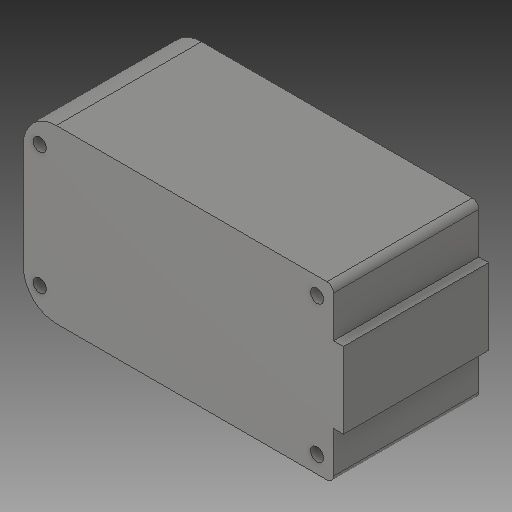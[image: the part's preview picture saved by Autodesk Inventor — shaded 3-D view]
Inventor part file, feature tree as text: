
AUTODESK INVENTOR PART (.ipt)
format: ipt  version: 2018 (Build 220112000, 112)  size: 108,032 bytes
history: native  units: mm
features: other x1, fillet x1
ambient origin geometry x8: Origin, YZ Plane, XZ Plane, XY Plane, X Axis, Y Axis, Z Axis, Center Point
bodies: Body1 (feature_tree)
feature tree (2):
  other  "Твердое тело1"
  fillet  "Fillet2"  [1 undecoded]
note: 1 required parameter value undecoded (feature->parameter linkage not recoverable at this tier; creation-order binding heuristic only, values carry confidence <= 0.55)
